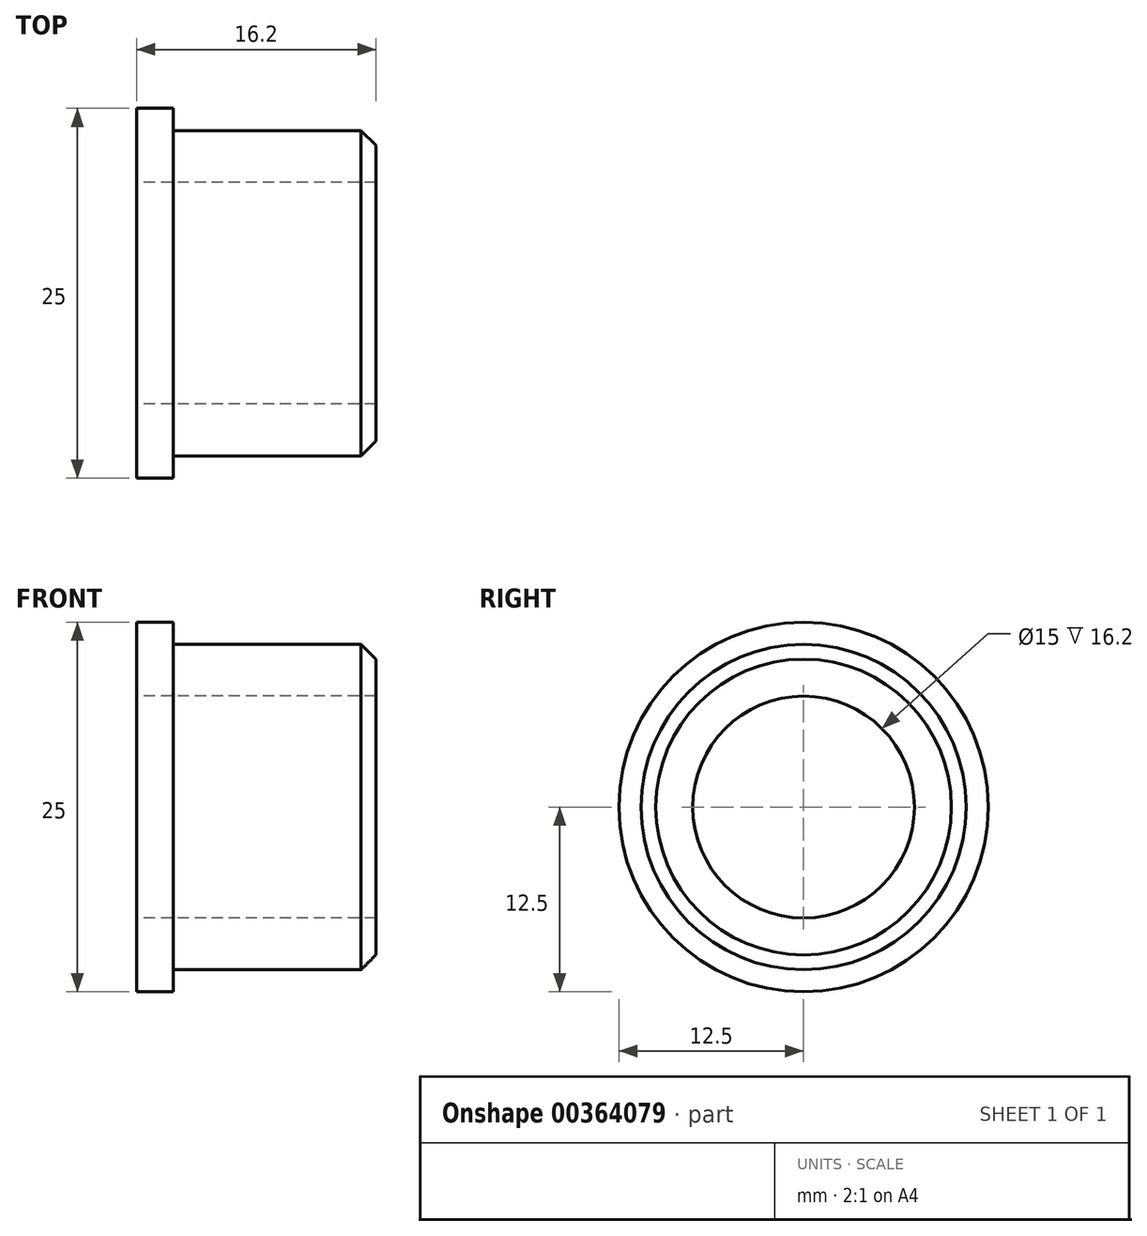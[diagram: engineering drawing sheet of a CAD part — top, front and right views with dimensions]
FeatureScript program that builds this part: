
annotation { "Feature Type Name" : "Feature", "Feature Type Description" : "" }
export const myFeature = defineFeature(function(context is Context, id is Id, definition is map)
    precondition{}
    {
        {
            var Q0;
            Q0=qCreatedBy(makeId("Top.planeOp"),FACE);
            var sketch = newSketch(context, id + "F0", { "sketchPlane" : qUnion([Q0])});
            skLineSegment(sketch, "E0", {"start": v(0, 0) * mm, "end": v(12.9, 0) * mm, "construction": true});
            skLineSegment(sketch, "E1", {"start": v(0, 7.5) * mm, "end": v(0, 12.5) * mm});
            skLineSegment(sketch, "E2", {"start": v(0, 12.5) * mm, "end": v(2.5, 12.5) * mm});
            skLineSegment(sketch, "E3", {"start": v(2.5, 12.5) * mm, "end": v(2.5, 11) * mm});
            skLineSegment(sketch, "E4", {"start": v(2.5, 11) * mm, "end": v(16.2, 11) * mm});
            skLineSegment(sketch, "E5", {"start": v(16.2, 11) * mm, "end": v(16.2, 7.5) * mm});
            skLineSegment(sketch, "E6", {"start": v(16.2, 7.5) * mm, "end": v(0, 7.5) * mm});
            skSolve(sketch);
        }
        {
            var Q0;
            Q0=makeQuery(id+"F0.imprint","IMPRINT",FACE,{"disambiguationData":[TD([[makeQuery(id+"F0.imprint","IMPRINT",EDGE,{"derivedFrom":sQuery(id+"F0.wireOp",EDGE,"E1")}),-1.0]])]});
            var Q1;
            Q1=sQuery(id+"F0.wireOp",EDGE,"E0");
            revolve(context, id + "F1", {"entities" : qUnion([Q0]), "axis" : qUnion([Q1]), "revolveType" : RevolveType.FULL});
        }
        {
            var Q0;
            Q0=makeQuery(id+"F1.opRevolve","SWEPT_EDGE",EDGE,{"disambiguationData":[OSD([sQuery(id+"F0.wireOp",EDGE,"E4"),sQuery(id+"F0.wireOp",EDGE,"E5")])]});
            chamfer(context, id + "F2", {"entities" : qUnion([Q0]), "width" : 1 * mm, "tangentPropagation" : true});
        }
    });
